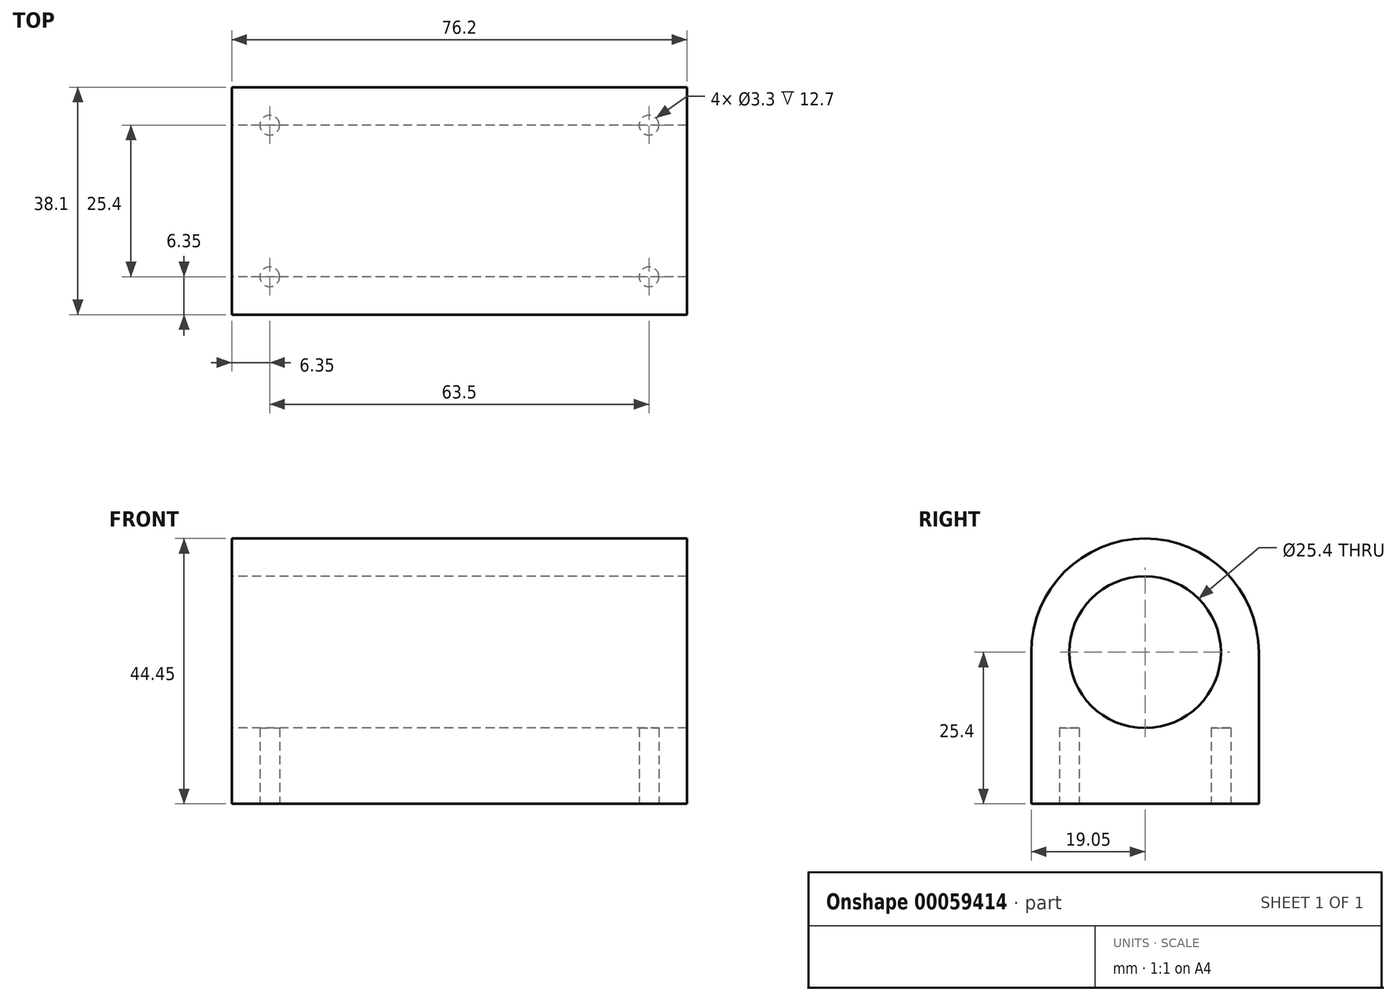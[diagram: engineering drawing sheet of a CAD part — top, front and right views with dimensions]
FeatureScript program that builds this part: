
annotation { "Feature Type Name" : "Feature", "Feature Type Description" : "" }
export const myFeature = defineFeature(function(context is Context, id is Id, definition is map)
    precondition{}
    {
        {
            var Q0;
            Q0=qCreatedBy(makeId("Right.planeOp"),FACE);
            var sketch = newSketch(context, id + "F0", { "sketchPlane" : qUnion([Q0])});
            skArc(sketch, "E0", {"start": v(19.05, 25.4) * mm, "mid": v(0, 44.45) * mm, "end": v(-19.05, 25.4) * mm});
            skCircle(sketch, "E1", {"center": v(0, 25.4) * mm, "radius": 12.7 * mm});
            skLineSegment(sketch, "E2", {"start": v(-19.05, 25.4) * mm, "end": v(-19.05, 0) * mm});
            skLineSegment(sketch, "E3", {"start": v(19.05, 25.4) * mm, "end": v(19.05, 0) * mm});
            skLineSegment(sketch, "E4", {"start": v(19.05, 0) * mm, "end": v(-19.05, 0) * mm});
            skSolve(sketch);
        }
        {
            var Q0;
            Q0 = qSketchRegion(id + "F0", true);
            extrude(context, id + "F1", {"entities" : qUnion([Q0]), "depth" : 38.1 * mm, "hasSecondDirection" : true, "secondDirectionOppositeDirection" : true, "secondDirectionDepth" : 38.1 * mm});
        }
        {
            var Q0;
            Q0=makeQuery(id+"F1.opExtrude","SWEPT_FACE",FACE,{"disambiguationData":[OSD([sQuery(id+"F0.wireOp",EDGE,"E4")])]});
            var sketch = newSketch(context, id + "F2", { "sketchPlane" : qUnion([Q0])});
            skLineSegment(sketch, "E5.bottom", {"start": v(-31.75, 12.7) * mm, "end": v(31.75, 12.7) * mm, "construction": true});
            skLineSegment(sketch, "E5.top", {"start": v(-31.75, -12.7) * mm, "end": v(31.75, -12.7) * mm, "construction": true});
            skLineSegment(sketch, "E5.left", {"start": v(-31.75, 12.7) * mm, "end": v(-31.75, -12.7) * mm, "construction": true});
            skLineSegment(sketch, "E5.right", {"start": v(31.75, 12.7) * mm, "end": v(31.75, -12.7) * mm, "construction": true});
            skCircle(sketch, "E6", {"center": v(-31.75, 12.7) * mm, "radius": 1.65 * mm});
            skCircle(sketch, "E7", {"center": v(-31.75, -12.7) * mm, "radius": 1.65 * mm});
            skCircle(sketch, "E8", {"center": v(31.75, 12.7) * mm, "radius": 1.65 * mm});
            skCircle(sketch, "E9", {"center": v(31.75, -12.7) * mm, "radius": 1.65 * mm});
            skSolve(sketch);
        }
        {
            var Q0;
            Q0 = qSketchRegion(id + "F2", true);
            extrude(context, id + "F3", {"entities" : qUnion([Q0]), "operationType" : NewBodyOperationType.REMOVE, "oppositeDirection" : true, "depth" : 12.7 * mm});
        }
    });
